# Revit family: Accessories_Set-Grohe-Essentials_Master-40344_Series
name_source: partatom
category: Specialty Equipment
revit_build: Autodesk Revit 2014 (Build: 20130308_1515(x64)
units: mm (PartAtom-declared; Revit-internal decimal feet)

## types (2) — shared parameters
Assembly Code = C1030200
Default Elevation = 43"
Description = Essentials Master bathroom accessories set 5-in-1
Height = 7 7/8"
Installation Type = Wall Mounted
Length = 25 3/4"
Manufacturer = Grohe
Price = Prices may vary. Please consult Manufacturer Representative for most up-to-date price list.
Product Page URL = https://www.grohe.us
Robe Hook 40364 = No
Soap Dish 40444 = Yes
Toilet Paper Holder 40367 = No
Towel Bar 40366 = No
Towel Ring 40365 = No
URL = https://www.grohe.us

## per-type parameters (varying)
| type | Finish | Material |
| 40344001 | Metal-Grohe-001-Chrome | Metal-Grohe-001-Chrome |
| 40344EN1 | Metal-Grohe-EN1-Brushed Nickel | Metal-Grohe-EN1-Brushed Nickel |

note: column(s) folded — value = type name in every type: Model

## geometry (parser evidence)
native form markers: Sweep x2
no freeform markers — native parametric forms only
